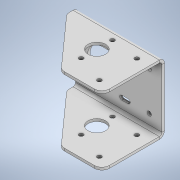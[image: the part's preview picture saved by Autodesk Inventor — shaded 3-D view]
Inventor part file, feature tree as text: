
AUTODESK INVENTOR PART (.ipt)
format: ipt  version: 2022 (Build 260153000, 153)  size: 246,784 bytes
history: native  units: in
note: dims shown in document units (in); Inventor stores cm internally (conversion verified against a paired STEP export)
features: sheet_metal_op x4, other x4, sketch x3, hole x2, chamfer x1
ambient origin geometry x8: Origin, YZ Plane, XZ Plane, XY Plane, X Axis, Y Axis, Z Axis, Center Point
bodies: Solid2 (feature_tree)
feature tree (14):
  sketch  "Sketch1"  dims[d1=2.1654in d2=0.7874in]
  sheet_metal_op  "Face1"
  hole  "Hole1"  [1 undecoded]
  sheet_metal_op  "Flange1"
  sketch  "Sketch3"  dims[d8=1.2205in d9=1.2205in d10=1.2205in d11=0.0669in d12=0.1969in d13=0.4724in d14=0.1969in d15=0.2362in d16=0.08in d17=0.1339in d18=0.2362in d19=0.2559in d20=0.1181in d21=0.6181in d22=0.08in d23=0.8108in d24=0.08in d25=0.04in d26=0.16in d27=0.08in d28=1.9685in d29=90.0deg d30=0.08in d31=0.32in d32=0.08in d33=0.08in d34=0.7874in d35=1.1811in d36=0.5512in d37=0.4921in d38=0.4921in d39=0.1969in d40=0.4921in d41=0.08in d42=0.0in d43=0.1339in d44=0.2362in d45=0.2559in d46=0.1181in d47=90.0deg d48=0.315in d49=0.8108in d50=0.08in d51=0.0in d52=0.2362in d53=2.7165in]
  hole  "Hole2"  [1 undecoded]
  chamfer  "Corner Round1"
  other  "Plate1"
  sketch  "Sketch2"  dims[d4=1.2205in d7=1.2205in]
  other  "Plate2"
  sheet_metal_op  "Bend1"
  sheet_metal_op  "Corner1"
  other  "Cut1"
  other  "Cut2"
note: 2 required parameter values undecoded (feature->parameter linkage not recoverable at this tier; creation-order binding heuristic only, values carry confidence <= 0.55)
